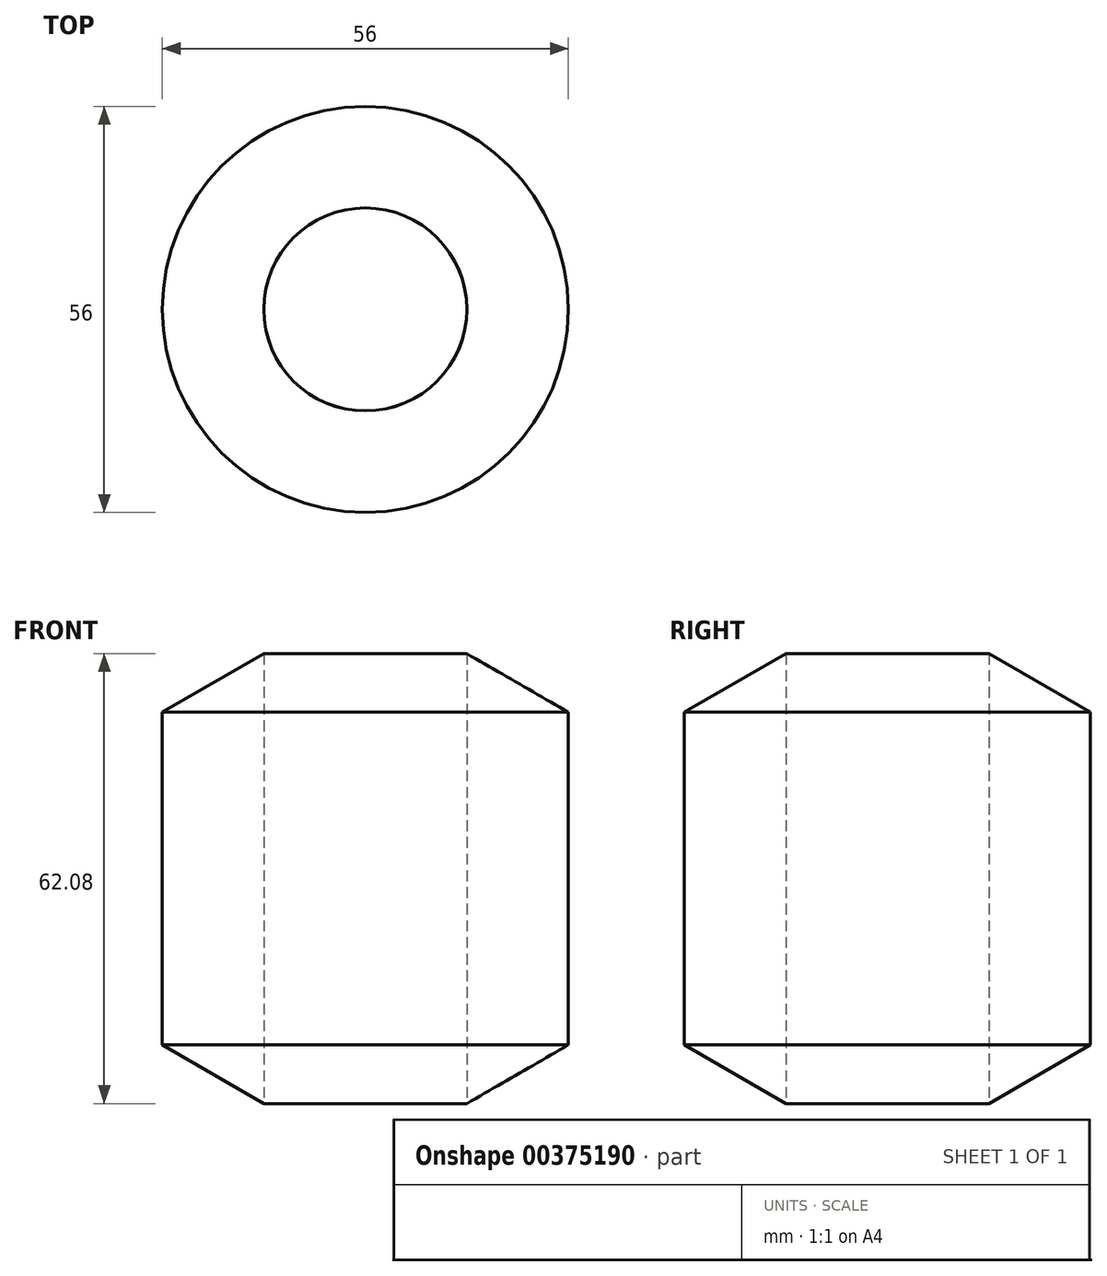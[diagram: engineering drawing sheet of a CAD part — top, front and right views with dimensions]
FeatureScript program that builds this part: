
annotation { "Feature Type Name" : "Feature", "Feature Type Description" : "" }
export const myFeature = defineFeature(function(context is Context, id is Id, definition is map)
    precondition{}
    {
        {
            var Q0;
            Q0=qCreatedBy(makeId("Top.planeOp"),FACE);
            var sketch = newSketch(context, id + "F0", { "sketchPlane" : qUnion([Q0])});
            skCircle(sketch, "E0", {"center": v(0, 0) * mm, "radius": 28 * mm});
            skCircle(sketch, "E1", {"center": v(0, 0) * mm, "radius": 14 * mm});
            skSolve(sketch);
        }
        {
            var Q0;
            Q0=makeQuery(id+"F0.imprint","IMPRINT",FACE,{"disambiguationData":[TD([[makeQuery(id+"F0.imprint","IMPRINT",EDGE,{"derivedFrom":sQuery(id+"F0.wireOp",EDGE,"E0")}),1.0]])]});
            extrude(context, id + "F1", {"entities" : qUnion([Q0]), "depth" : (59.16 + 2.92) * mm, "symmetric" : true});
        }
        {
            var Q0;
            Q0=qCreatedBy(makeId("Front.planeOp"),FACE);
            var sketch = newSketch(context, id + "F2", { "sketchPlane" : qUnion([Q0])});
            skLineSegment(sketch, "E2", {"start": v(14, 31.04) * mm, "end": v(28, 22.96) * mm});
            skLineSegment(sketch, "E3", {"start": v(28, 22.96) * mm, "end": v(28, 31.04) * mm});
            skLineSegment(sketch, "E4", {"start": v(28, 31.04) * mm, "end": v(14, 31.04) * mm});
            skLineSegment(sketch, "E5", {"start": v(-33.57, 0) * mm, "end": v(41.06, 0) * mm, "construction": true});
            skLineSegment(sketch, "E6.MirrorCS", {"start": v(14, -31.04) * mm, "end": v(28, -22.96) * mm});
            skLineSegment(sketch, "E7.MirrorCS", {"start": v(28, -22.96) * mm, "end": v(28, -31.04) * mm});
            skLineSegment(sketch, "E8.MirrorCS", {"start": v(28, -31.04) * mm, "end": v(14, -31.04) * mm});
            skSolve(sketch);
        }
        {
            var Q0;
            Q0 = qSketchRegion(id + "F2", true);
            var Q1;
            Q1=makeQuery(id+"F1.opExtrude","CAP_EDGE",EDGE,{"disambiguationData":[OSD([sQuery(id+"F0.wireOp",EDGE,"E1")])],"isStart":false});
            revolve(context, id + "F3", {"operationType" : NewBodyOperationType.REMOVE, "entities" : qUnion([Q0]), "axis" : qUnion([Q1]), "revolveType" : RevolveType.FULL, "oppositeDirection" : true});
        }
    });
